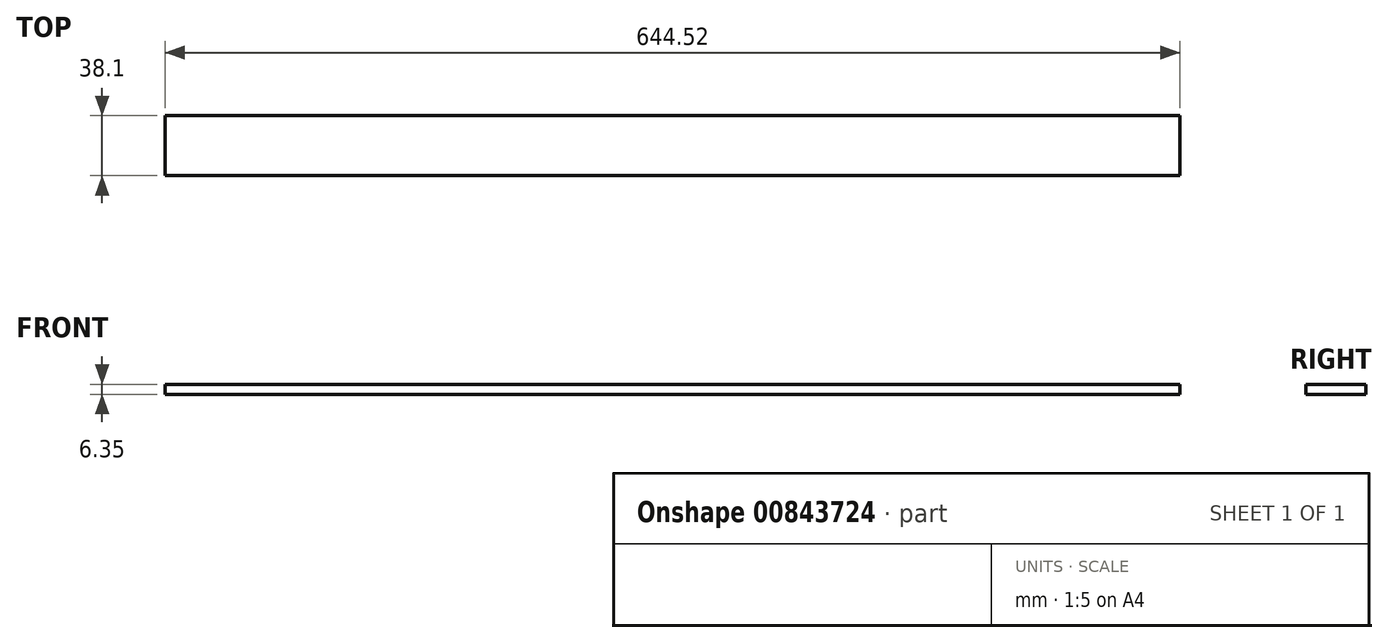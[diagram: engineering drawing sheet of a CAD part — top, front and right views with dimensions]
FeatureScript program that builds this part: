
annotation { "Feature Type Name" : "Feature", "Feature Type Description" : "" }
export const myFeature = defineFeature(function(context is Context, id is Id, definition is map)
    precondition{}
    {
        {
            var Q0;
            Q0=qCreatedBy(makeId("Top.planeOp"),FACE);
            var sketch = newSketch(context, id + "F0", { "sketchPlane" : qUnion([Q0])});
            skLineSegment(sketch, "E0.bottom", {"start": v(322.26, 19.05) * mm, "end": v(-322.26, 19.05) * mm});
            skLineSegment(sketch, "E0.top", {"start": v(322.26, -19.05) * mm, "end": v(-322.26, -19.05) * mm});
            skLineSegment(sketch, "E0.left", {"start": v(322.26, 19.05) * mm, "end": v(322.26, -19.05) * mm});
            skLineSegment(sketch, "E0.right", {"start": v(-322.26, 19.05) * mm, "end": v(-322.26, -19.05) * mm});
            skPoint(sketch, "E0.middle", {"position": v(0, 0) * mm});
            skSolve(sketch);
        }
        {
            var Q0;
            Q0=qSketchRegion(id+"F0",true);
            extrude(context, id + "F1", {"entities" : qUnion([Q0]), "depth" : 6.35 * mm, "offsetDistance" : 25.4 * mm});
        }
    });
